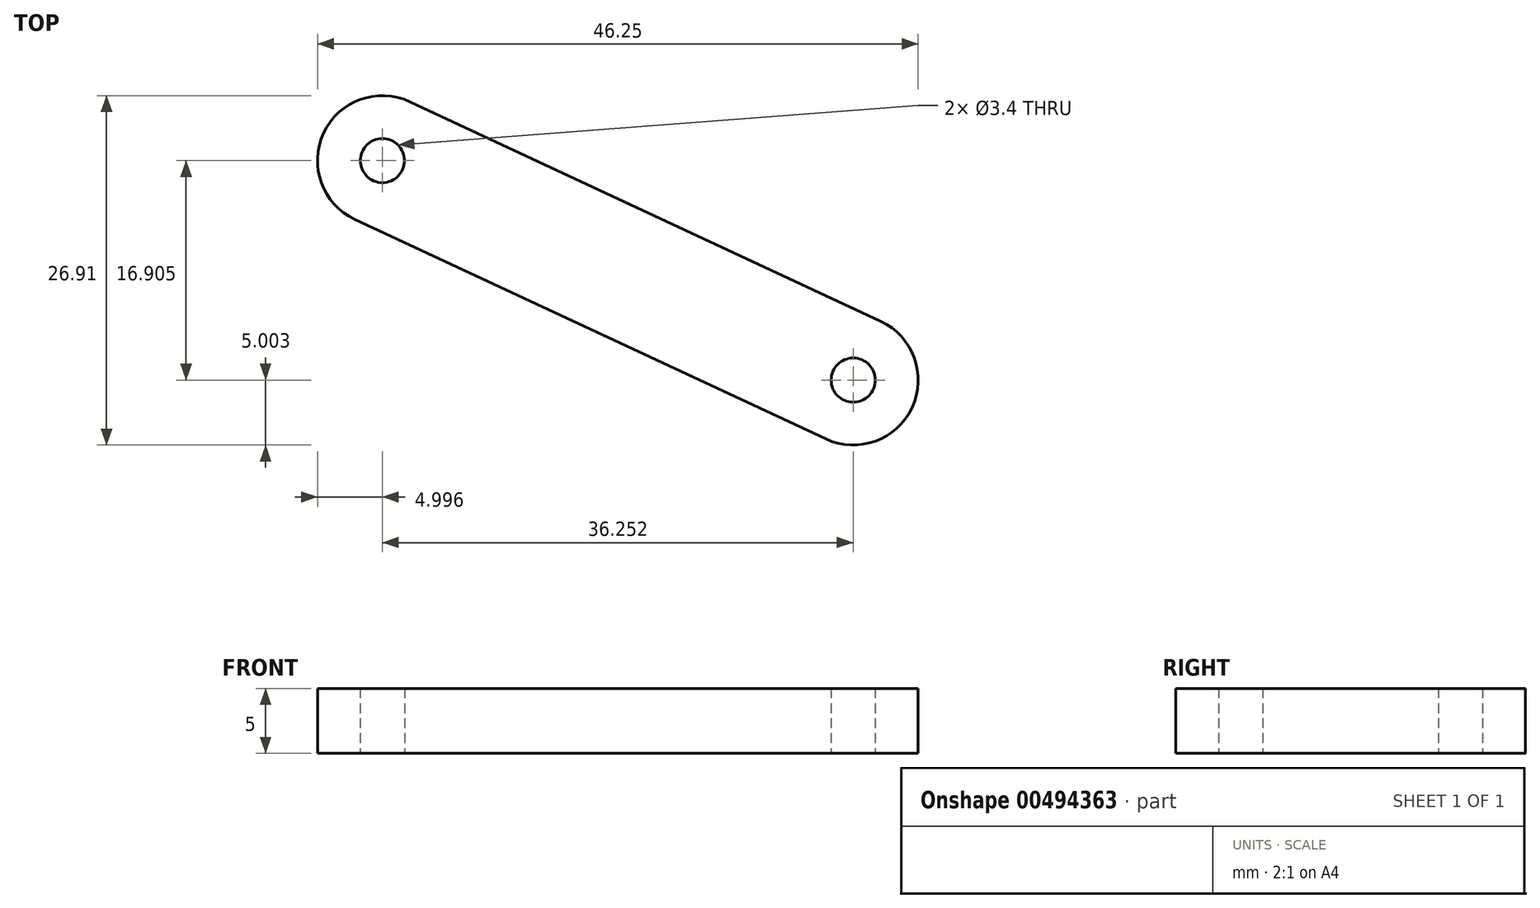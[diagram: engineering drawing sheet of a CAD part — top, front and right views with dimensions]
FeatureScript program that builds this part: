
annotation { "Feature Type Name" : "Feature", "Feature Type Description" : "" }
export const myFeature = defineFeature(function(context is Context, id is Id, definition is map)
    precondition{}
    {
        {
            var Q0;
            Q0=qCreatedBy(makeId("Top.planeOp"),FACE);
            var sketch = newSketch(context, id + "F0", { "sketchPlane" : qUnion([Q0])});
            skLineSegment(sketch, "E0.left", {"start": v(-52.76, 28.84) * mm, "end": v(-52.76, -11.16) * mm});
            skLineSegment(sketch, "E0.right", {"start": v(-42.76, 28.84) * mm, "end": v(-42.76, -11.16) * mm});
            skArc(sketch, "E1", {"start": v(-52.76, 28.84) * mm, "mid": v(-47.76, 33.84) * mm, "end": v(-42.76, 28.84) * mm});
            skArc(sketch, "E2", {"start": v(-52.76, -11.16) * mm, "mid": v(-47.76, -16.16) * mm, "end": v(-42.76, -11.16) * mm});
            skCircle(sketch, "E3", {"center": v(-47.76, -11.16) * mm, "radius": 1.7 * mm});
            skCircle(sketch, "E4", {"center": v(-47.76, 28.84) * mm, "radius": 1.7 * mm});
            skLineSegment(sketch, "E5", {"start": v(-52.76, -5.66) * mm, "end": v(-42.76, -5.66) * mm});
            skSolve(sketch);
        }
        {
            var Q0;
            Q0 = qSketchRegion(id + "F0", true);
            extrude(context, id + "F1", {"entities" : qUnion([Q0]), "depth" : 5 * mm});
        }
        {
            var Q0;
            Q0=makeQuery(id+"F1.opExtrude","SWEPT_BODY",BODY,{"disambiguationData":[OSD([sQuery(id+"F0.wireOp",EDGE,"E0.left"),sQuery(id+"F0.wireOp",EDGE,"E0.right"),sQuery(id+"F0.wireOp",EDGE,"E1"),sQuery(id+"F0.wireOp",EDGE,"E2"),sQuery(id+"F0.wireOp",EDGE,"E3"),sQuery(id+"F0.wireOp",EDGE,"E4")])]});
            var Q1;
            Q1=makeQuery(id+"F1.opExtrude","CAP_EDGE",EDGE,{"disambiguationData":[OSD([sQuery(id+"F0.wireOp",EDGE,"E3")])],"isStart":false});
            transform(context, id + "F2", {"entities" : qUnion([Q0]), "transformType" : TransformType.ROTATION, "transformAxis" : qUnion([Q1]), "angle" : 115 * degree, "oppositeDirection" : true, "makeCopy" : false});
        }
    });
